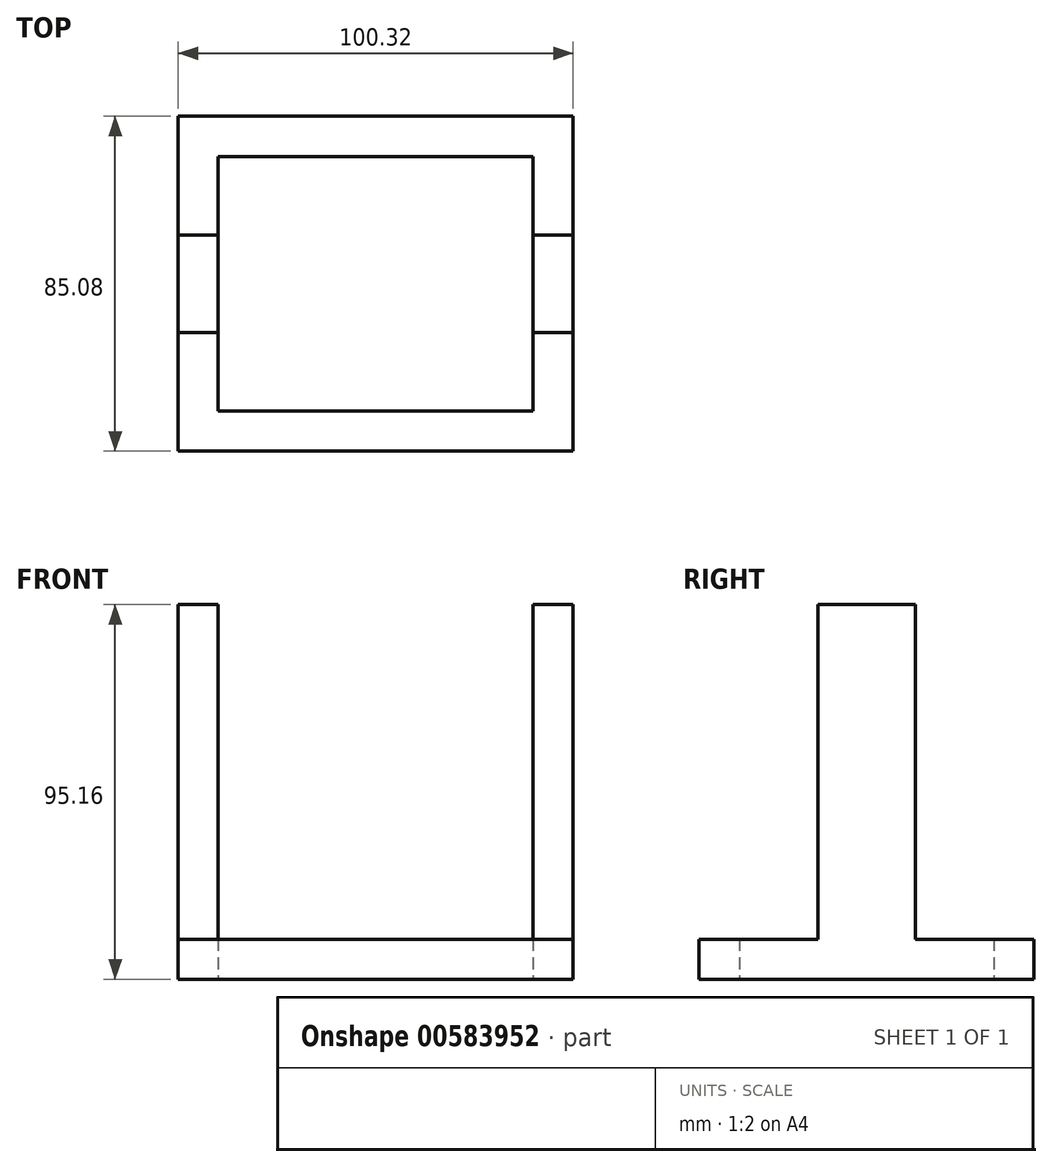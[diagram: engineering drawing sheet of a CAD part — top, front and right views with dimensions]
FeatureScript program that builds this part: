
annotation { "Feature Type Name" : "Feature", "Feature Type Description" : "" }
export const myFeature = defineFeature(function(context is Context, id is Id, definition is map)
    precondition{}
    {
        {
            var Q0;
            Q0=qCreatedBy(makeId("Top.planeOp"),FACE);
            var sketch = newSketch(context, id + "F0", { "sketchPlane" : qUnion([Q0])});
            skLineSegment(sketch, "E0.bottom", {"start": v(-50.16, 42.54) * mm, "end": v(50.16, 42.54) * mm});
            skLineSegment(sketch, "E0.top", {"start": v(-50.16, -42.54) * mm, "end": v(50.16, -42.54) * mm});
            skLineSegment(sketch, "E0.left", {"start": v(-50.16, 42.54) * mm, "end": v(-50.16, -42.54) * mm});
            skLineSegment(sketch, "E0.right", {"start": v(50.16, 42.54) * mm, "end": v(50.16, -42.54) * mm});
            skPoint(sketch, "E0.middle", {"position": v(0, 0) * mm});
            skSolve(sketch);
        }
        {
            var Q0;
            Q0=makeQuery(id+"F0.imprint","IMPRINT",FACE,{"disambiguationData":[TD([[makeQuery(id+"F0.imprint","IMPRINT",EDGE,{"derivedFrom":sQuery(id+"F0.wireOp",EDGE,"E0.bottom")}),-1.0]])]});
            var sketch = newSketch(context, id + "F1", { "sketchPlane" : qUnion([Q0])});
            skLineSegment(sketch, "E1.bottom", {"start": v(-40, 32.34) * mm, "end": v(40, 32.34) * mm});
            skLineSegment(sketch, "E1.top", {"start": v(-40, -32.34) * mm, "end": v(40, -32.34) * mm});
            skLineSegment(sketch, "E1.left", {"start": v(-40, 32.34) * mm, "end": v(-40, -32.34) * mm});
            skLineSegment(sketch, "E1.right", {"start": v(40, 32.34) * mm, "end": v(40, -32.34) * mm});
            skPoint(sketch, "E1.middle", {"position": v(0, 0) * mm});
            skSolve(sketch);
        }
        {
            var Q0;
            Q0=makeQuery(id+"F0.imprint","IMPRINT",FACE,{"disambiguationData":[TD([[makeQuery(id+"F0.imprint","IMPRINT",EDGE,{"derivedFrom":sQuery(id+"F0.wireOp",EDGE,"E0.bottom")}),-1.0]])]});
            extrude(context, id + "F2", {"entities" : qUnion([Q0]), "depth" : 95.16 * mm, "offsetDistance" : 25.4 * mm});
        }
        {
            var Q0;
            Q0=makeQuery(id+"F1.imprint","IMPRINT",FACE,{"disambiguationData":[TD([[makeQuery(id+"F1.imprint","IMPRINT",EDGE,{"derivedFrom":sQuery(id+"F1.wireOp",EDGE,"E1.bottom")}),-1.0]])]});
            extrude(context, id + "F3", {"entities" : qUnion([Q0]), "operationType" : NewBodyOperationType.REMOVE, "depth" : 85 * mm, "offsetDistance" : 25.4 * mm});
        }
        {
            var Q0;
            Q0=makeQuery(id+"F2.opExtrude","CAP_FACE",FACE,{"disambiguationData":[OSD([sQuery(id+"F0.wireOp",EDGE,"E0.bottom"),sQuery(id+"F0.wireOp",EDGE,"E0.top"),sQuery(id+"F0.wireOp",EDGE,"E0.left"),sQuery(id+"F0.wireOp",EDGE,"E0.right")])],"isStart":false});
            var sketch = newSketch(context, id + "F4", { "sketchPlane" : qUnion([Q0])});
            skLineSegment(sketch, "E2.bottom", {"start": v(-40, 32.34) * mm, "end": v(40, 32.34) * mm});
            skLineSegment(sketch, "E2.top", {"start": v(-40, -32.34) * mm, "end": v(40, -32.34) * mm});
            skLineSegment(sketch, "E2.left", {"start": v(-40, 32.34) * mm, "end": v(-40, -32.34) * mm});
            skLineSegment(sketch, "E2.right", {"start": v(40, 32.34) * mm, "end": v(40, -32.34) * mm});
            skLineSegment(sketch, "E3.top", {"start": v(-40, 42.54) * mm, "end": v(40, 42.54) * mm});
            skLineSegment(sketch, "E3.left", {"start": v(-40, 32.34) * mm, "end": v(-40, 42.54) * mm});
            skLineSegment(sketch, "E3.right", {"start": v(40, 32.34) * mm, "end": v(40, 42.54) * mm});
            skPoint(sketch, "E4.oppositeSnap0", {"position": v(40, 37.44) * mm});
            skLineSegment(sketch, "E4.top", {"start": v(-40, -42.54) * mm, "end": v(40, -42.54) * mm});
            skLineSegment(sketch, "E4.left", {"start": v(-40, -32.34) * mm, "end": v(-40, -42.54) * mm});
            skLineSegment(sketch, "E4.right", {"start": v(40, -32.34) * mm, "end": v(40, -42.54) * mm});
            skSolve(sketch);
        }
        {
            var Q0;
            Q0=makeQuery(id+"F4.imprint","IMPRINT",FACE,{"disambiguationData":[TD([[makeQuery(id+"F4.imprint","IMPRINT",EDGE,{"derivedFrom":sQuery(id+"F4.wireOp",EDGE,"E2.top")}),-1.0]])]});
            var Q1;
            Q1=makeQuery(id+"F4.imprint","IMPRINT",FACE,{"disambiguationData":[TD([[makeQuery(id+"F4.imprint","IMPRINT",EDGE,{"derivedFrom":sQuery(id+"F4.wireOp",EDGE,"E2.bottom")}),1.0]])]});
            var Q2;
            Q2=makeQuery(id+"F4.imprint","IMPRINT",FACE,{"disambiguationData":[TD([[makeQuery(id+"F4.imprint","IMPRINT",EDGE,{"derivedFrom":sQuery(id+"F4.wireOp",EDGE,"E2.left")}),1.0]])]});
            extrude(context, id + "F5", {"entities" : qUnion([Q0, Q1, Q2]), "operationType" : NewBodyOperationType.REMOVE, "oppositeDirection" : true, "depth" : 74.84 * mm, "offsetDistance" : 25.4 * mm});
        }
        {
            var Q0;
            Q0=makeQuery(id+"F2.opExtrude","SWEPT_FACE",FACE,{"disambiguationData":[OSD([sQuery(id+"F0.wireOp",EDGE,"E0.left")])]});
            var sketch = newSketch(context, id + "F6", { "sketchPlane" : qUnion([Q0])});
            skLineSegment(sketch, "E5.bottom", {"start": v(-42.54, 0) * mm, "end": v(42.54, 0) * mm});
            skLineSegment(sketch, "E5.top", {"start": v(-42.54, 10.16) * mm, "end": v(42.54, 10.16) * mm});
            skLineSegment(sketch, "E5.left", {"start": v(-42.54, 0) * mm, "end": v(-42.54, 10.16) * mm});
            skLineSegment(sketch, "E5.right", {"start": v(42.54, 0) * mm, "end": v(42.54, 10.16) * mm});
            skLineSegment(sketch, "E6.bottom", {"start": v(-42.54, 10.16) * mm, "end": v(-22.54, 10.16) * mm});
            skLineSegment(sketch, "E6.top", {"start": v(-42.54, 95.16) * mm, "end": v(-22.54, 95.16) * mm});
            skLineSegment(sketch, "E6.left", {"start": v(-42.54, 10.16) * mm, "end": v(-42.54, 95.16) * mm});
            skLineSegment(sketch, "E6.right", {"start": v(-22.54, 10.16) * mm, "end": v(-22.54, 95.16) * mm});
            skLineSegment(sketch, "E7.bottom", {"start": v(42.54, 10.16) * mm, "end": v(22.54, 10.16) * mm});
            skLineSegment(sketch, "E7.top", {"start": v(42.54, 95.16) * mm, "end": v(22.54, 95.16) * mm});
            skLineSegment(sketch, "E7.left", {"start": v(42.54, 10.16) * mm, "end": v(42.54, 95.16) * mm});
            skLineSegment(sketch, "E7.right", {"start": v(22.54, 10.16) * mm, "end": v(22.54, 95.16) * mm});
            skLineSegment(sketch, "E8.bottom", {"start": v(-22.54, 95.16) * mm, "end": v(-12.38, 95.16) * mm});
            skLineSegment(sketch, "E8.top", {"start": v(-22.54, 10.16) * mm, "end": v(-12.38, 10.16) * mm});
            skLineSegment(sketch, "E8.left", {"start": v(-22.54, 95.16) * mm, "end": v(-22.54, 10.16) * mm});
            skLineSegment(sketch, "E8.right", {"start": v(-12.38, 95.16) * mm, "end": v(-12.38, 10.16) * mm});
            skLineSegment(sketch, "E9.bottom", {"start": v(22.54, 95.16) * mm, "end": v(12.38, 95.16) * mm});
            skLineSegment(sketch, "E9.top", {"start": v(22.54, 10.16) * mm, "end": v(12.38, 10.16) * mm});
            skLineSegment(sketch, "E9.left", {"start": v(22.54, 95.16) * mm, "end": v(22.54, 10.16) * mm});
            skLineSegment(sketch, "E9.right", {"start": v(12.38, 95.16) * mm, "end": v(12.38, 10.16) * mm});
            skLineSegment(sketch, "E10.bottom", {"start": v(-12.33, 95.62) * mm, "end": v(12.33, 95.62) * mm});
            skLineSegment(sketch, "E10.top", {"start": v(-12.33, 85.46) * mm, "end": v(12.33, 85.46) * mm});
            skLineSegment(sketch, "E10.left", {"start": v(12.33, 95.62) * mm, "end": v(12.33, 85.46) * mm});
            skLineSegment(sketch, "E10.right", {"start": v(-12.33, 95.62) * mm, "end": v(-12.33, 85.46) * mm});
            skSolve(sketch);
        }
        {
            var Q0;
            Q0=makeQuery(id+"F6.imprint","IMPRINT",FACE,{"disambiguationData":[TD([[makeQuery(id+"F6.imprint","IMPRINT",EDGE,{"derivedFrom":sQuery(id+"F6.wireOp",EDGE,"E6.bottom")}),1.0]])]});
            var Q1;
            Q1=makeQuery(id+"F6.imprint","IMPRINT",FACE,{"disambiguationData":[TD([[makeQuery(id+"F6.imprint","IMPRINT",EDGE,{"derivedFrom":sQuery(id+"F6.wireOp",EDGE,"E5.top")}),1.0]])]});
            var Q2;
            Q2=makeQuery(id+"F6.imprint","IMPRINT",FACE,{"disambiguationData":[TD([[makeQuery(id+"F6.imprint","IMPRINT",EDGE,{"derivedFrom":sQuery(id+"F6.wireOp",EDGE,"E7.bottom")}),-1.0]])]});
            extrude(context, id + "F7", {"entities" : qUnion([Q0, Q1, Q2]), "operationType" : NewBodyOperationType.REMOVE, "endBound" : BoundingType.THROUGH_ALL, "oppositeDirection" : true, "depth" : 25.4 * mm, "offsetDistance" : 25.4 * mm});
        }
    });
